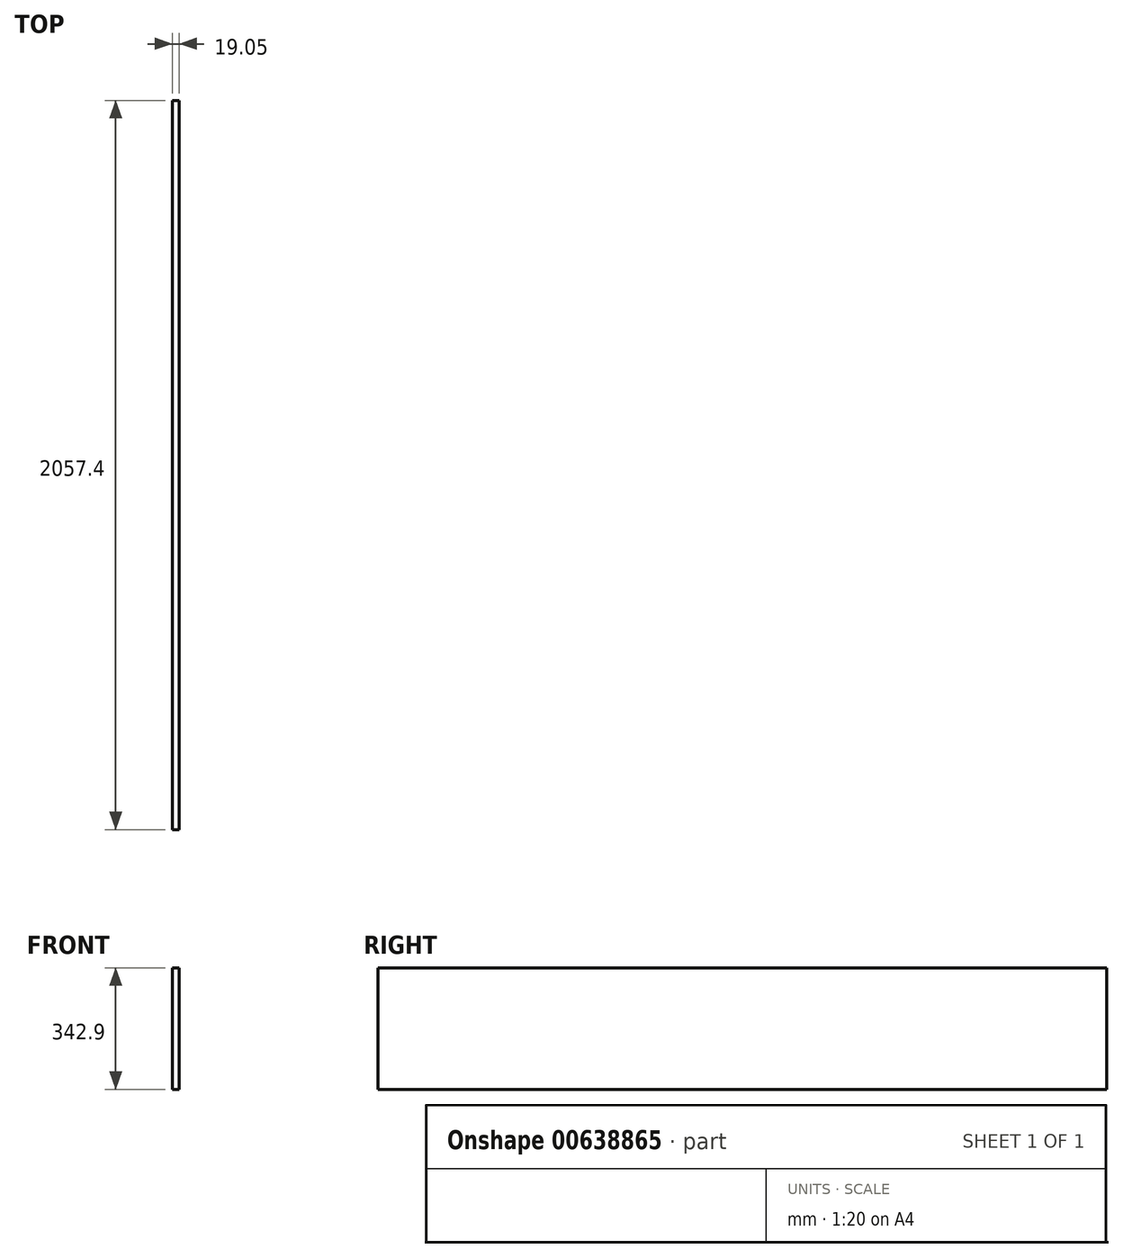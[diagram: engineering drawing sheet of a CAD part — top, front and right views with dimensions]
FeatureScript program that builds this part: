
annotation { "Feature Type Name" : "Feature", "Feature Type Description" : "" }
export const myFeature = defineFeature(function(context is Context, id is Id, definition is map)
    precondition{}
    {
        {
            var Q0;
            Q0=qCreatedBy(makeId("Right.planeOp"),FACE);
            var sketch = newSketch(context, id + "F0", { "sketchPlane" : qUnion([Q0])});
            skLineSegment(sketch, "E0.bottom", {"start": v(1028.7, 171.45) * mm, "end": v(-1028.7, 171.45) * mm});
            skLineSegment(sketch, "E0.top", {"start": v(1028.7, -171.45) * mm, "end": v(-1028.7, -171.45) * mm});
            skLineSegment(sketch, "E0.left", {"start": v(1028.7, 171.45) * mm, "end": v(1028.7, -171.45) * mm});
            skLineSegment(sketch, "E0.right", {"start": v(-1028.7, 171.45) * mm, "end": v(-1028.7, -171.45) * mm});
            skPoint(sketch, "E0.middle", {"position": v(0, 0) * mm});
            skSolve(sketch);
        }
        {
            var Q0;
            Q0 = qSketchRegion(id + "F0", true);
            extrude(context, id + "F1", {"entities" : qUnion([Q0]), "depth" : 19.05 * mm, "offsetDistance" : 25.4 * mm});
        }
    });
